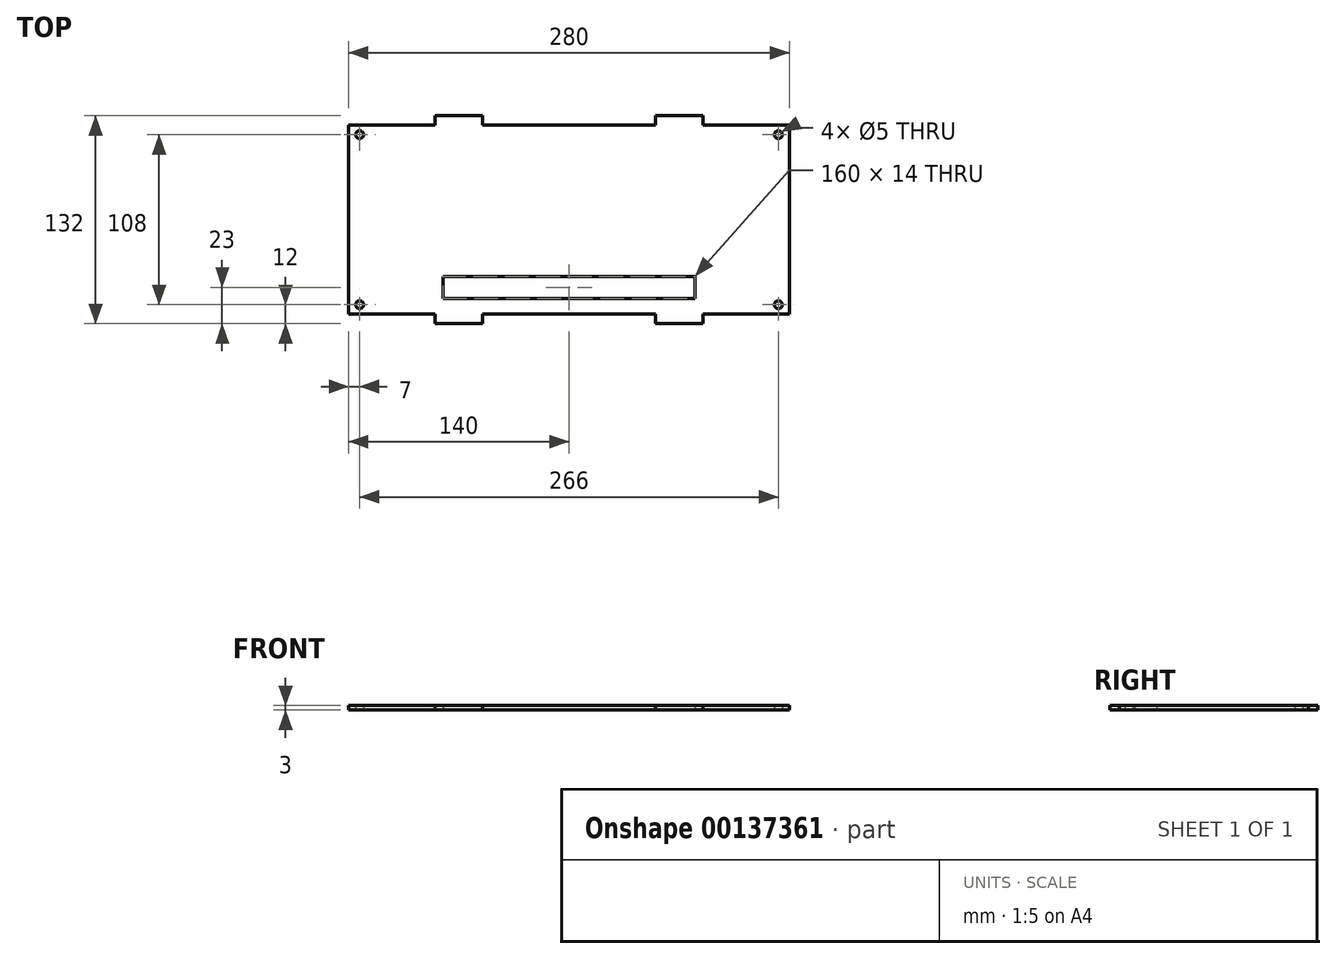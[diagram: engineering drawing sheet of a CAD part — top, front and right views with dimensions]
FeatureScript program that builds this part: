
annotation { "Feature Type Name" : "Feature", "Feature Type Description" : "" }
export const myFeature = defineFeature(function(context is Context, id is Id, definition is map)
    precondition{}
    {
        {
            var Q0;
            Q0=qCreatedBy(makeId("Top.planeOp"),FACE);
            var sketch = newSketch(context, id + "F0", { "sketchPlane" : qUnion([Q0])});
            skLineSegment(sketch, "E0.bottom", {"start": v(140, 60) * mm, "end": v(85, 60) * mm});
            skLineSegment(sketch, "E0.top", {"start": v(140, -60) * mm, "end": v(85, -60) * mm});
            skLineSegment(sketch, "E0.left", {"start": v(140, 60) * mm, "end": v(140, -60) * mm});
            skLineSegment(sketch, "E0.right", {"start": v(-140, 60) * mm, "end": v(-140, -60) * mm});
            skPoint(sketch, "E0.middle", {"position": v(0, 0) * mm});
            skLineSegment(sketch, "E1", {"start": v(-140, -60) * mm, "end": v(-133, -60) * mm, "construction": true});
            skLineSegment(sketch, "E2", {"start": v(-133, -60) * mm, "end": v(-133, -54) * mm, "construction": true});
            skCircle(sketch, "E3", {"center": v(-133, -54) * mm, "radius": 2.5 * mm});
            skCircle(sketch, "E4.MirrorC", {"center": v(-133, 54) * mm, "radius": 2.5 * mm});
            skCircle(sketch, "E5.MirrorC", {"center": v(133, 54) * mm, "radius": 2.5 * mm});
            skCircle(sketch, "E6.MirrorC", {"center": v(133, -54) * mm, "radius": 2.5 * mm});
            skLineSegment(sketch, "E7", {"start": v(0, -60) * mm, "end": v(0, -50) * mm, "construction": true});
            skLineSegment(sketch, "E8", {"start": v(0, -50) * mm, "end": v(-15, -50) * mm});
            skLineSegment(sketch, "E9", {"start": v(15, -50) * mm, "end": v(0, -50) * mm});
            skLineSegment(sketch, "E10", {"start": v(0, -50) * mm, "end": v(80, -50) * mm, "construction": true});
            skPoint(sketch, "E10.endSnap0", {"position": v(7.5, -50) * mm});
            skLineSegment(sketch, "E11", {"start": v(0, -50) * mm, "end": v(-80, -50) * mm, "construction": true});
            skPoint(sketch, "E11.endSnap0", {"position": v(-7.5, -50) * mm});
            skLineSegment(sketch, "E12", {"start": v(0, -50) * mm, "end": v(-80, -50) * mm});
            skLineSegment(sketch, "E13", {"start": v(-80, -50) * mm, "end": v(-80, -36) * mm});
            skLineSegment(sketch, "E14", {"start": v(-80, -36) * mm, "end": v(80, -36) * mm});
            skLineSegment(sketch, "E15", {"start": v(80, -36) * mm, "end": v(80, -50) * mm});
            skLineSegment(sketch, "E16", {"start": v(0, -50) * mm, "end": v(80, -50) * mm});
            skLineSegment(sketch, "E17", {"start": v(0, -60) * mm, "end": v(-55, -60) * mm, "construction": true});
            skLineSegment(sketch, "E18", {"start": v(-55, -60) * mm, "end": v(-55, -66) * mm});
            skLineSegment(sketch, "E19", {"start": v(-55, -66) * mm, "end": v(-85, -66) * mm});
            skLineSegment(sketch, "E20", {"start": v(-85, -66) * mm, "end": v(-85, -60) * mm});
            skLineSegment(sketch, "E21.trimOffspring", {"start": v(-85, -60) * mm, "end": v(-140, -60) * mm});
            skLineSegment(sketch, "E22", {"start": v(0, -60) * mm, "end": v(55, -60) * mm, "construction": true});
            skLineSegment(sketch, "E23", {"start": v(55, -60) * mm, "end": v(55, -66) * mm});
            skLineSegment(sketch, "E24", {"start": v(55, -66) * mm, "end": v(85, -66) * mm});
            skLineSegment(sketch, "E25", {"start": v(85, -66) * mm, "end": v(85, -60) * mm});
            skLineSegment(sketch, "E26.trimOffspring", {"start": v(55, -60) * mm, "end": v(-55, -60) * mm});
            skLineSegment(sketch, "E27", {"start": v(-140, 0) * mm, "end": v(140, 0) * mm, "construction": true});
            skLineSegment(sketch, "E28.MirrorCS", {"start": v(0, 60) * mm, "end": v(55, 60) * mm, "construction": true});
            skLineSegment(sketch, "E29.MirrorCS", {"start": v(0, 60) * mm, "end": v(-55, 60) * mm, "construction": true});
            skLineSegment(sketch, "E30", {"start": v(55, 60) * mm, "end": v(55, 66) * mm});
            skLineSegment(sketch, "E31", {"start": v(55, 66) * mm, "end": v(85, 66) * mm});
            skLineSegment(sketch, "E32", {"start": v(85, 66) * mm, "end": v(85, 60) * mm});
            skLineSegment(sketch, "E33", {"start": v(-55, 60) * mm, "end": v(-55, 66) * mm});
            skLineSegment(sketch, "E34", {"start": v(-55, 66) * mm, "end": v(-85, 66) * mm});
            skLineSegment(sketch, "E35", {"start": v(-85, 66) * mm, "end": v(-85, 60) * mm});
            skLineSegment(sketch, "E36.trimOffspring", {"start": v(-85, 60) * mm, "end": v(-140, 60) * mm});
            skLineSegment(sketch, "E37.trimOffspring", {"start": v(55, 60) * mm, "end": v(-55, 60) * mm});
            skSolve(sketch);
        }
        {
            var Q0;
            Q0=makeQuery(id+"F0.imprint","IMPRINT",FACE,{"disambiguationData":[TD([[makeQuery(id+"F0.imprint","IMPRINT",EDGE,{"derivedFrom":sQuery(id+"F0.wireOp",EDGE,"E0.bottom")}),1.0]])]});
            extrude(context, id + "F1", {"entities" : qUnion([Q0]), "endBound" : BoundingType.SYMMETRIC, "depth" : 3 * mm});
        }
    });
